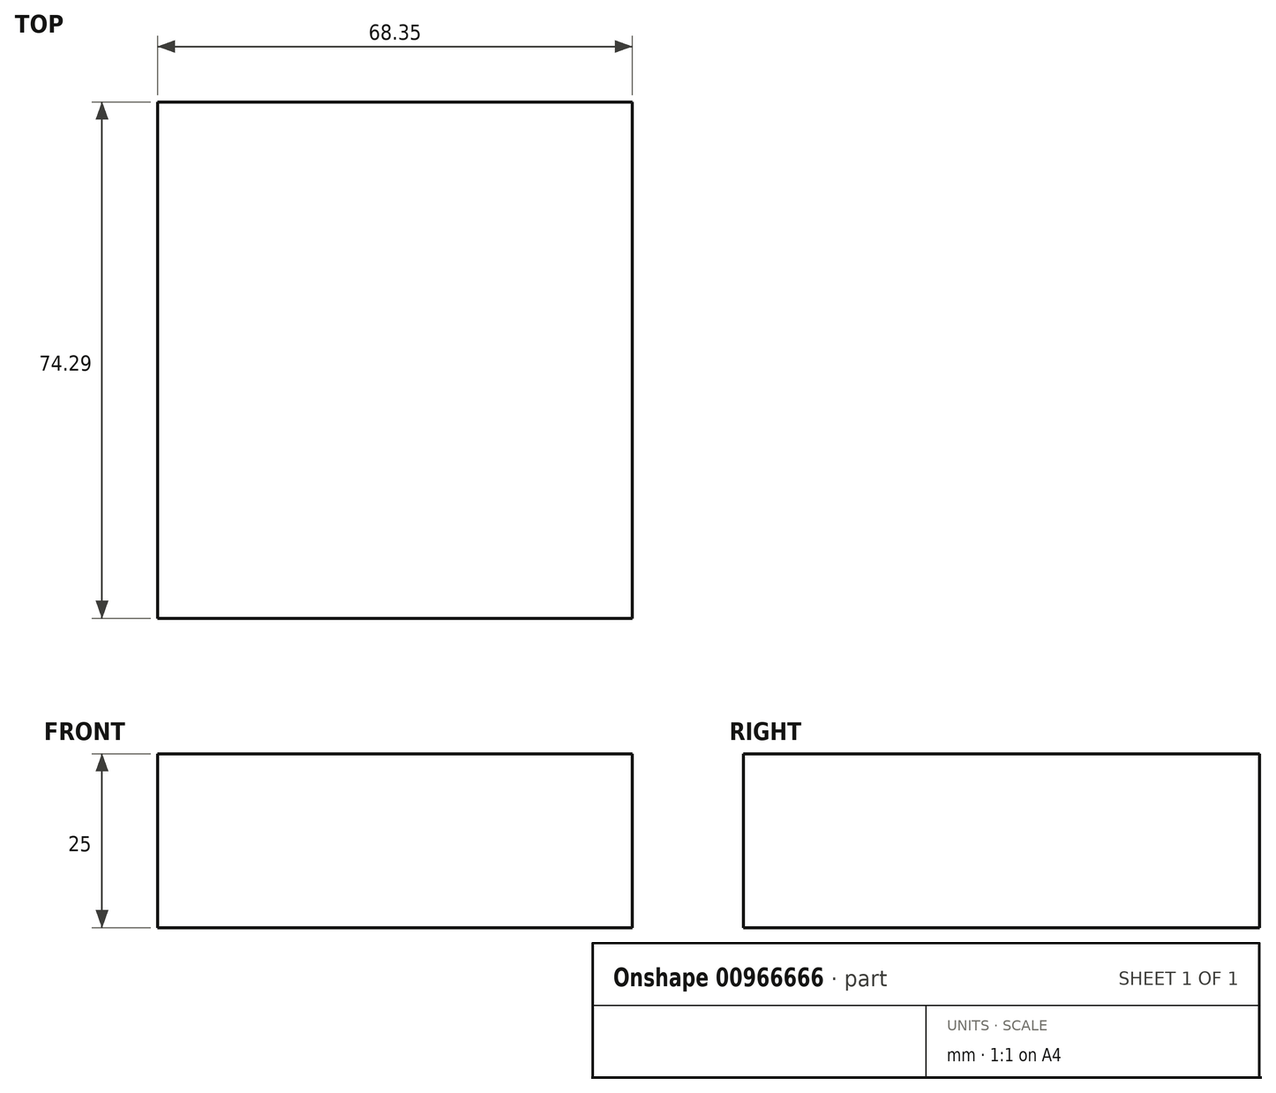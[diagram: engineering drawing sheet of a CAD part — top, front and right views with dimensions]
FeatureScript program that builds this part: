
annotation { "Feature Type Name" : "Feature", "Feature Type Description" : "" }
export const myFeature = defineFeature(function(context is Context, id is Id, definition is map)
    precondition{}
    {
        {
            var Q0;
            Q0=qCreatedBy(makeId("Top.planeOp"),FACE);
            var sketch = newSketch(context, id + "F0", { "sketchPlane" : qUnion([Q0])});
            skLineSegment(sketch, "E0.bottom", {"start": v(-29.84, 33.3) * mm, "end": v(38.5, 33.3) * mm});
            skLineSegment(sketch, "E0.top", {"start": v(-29.84, -40.98) * mm, "end": v(38.5, -40.98) * mm});
            skLineSegment(sketch, "E0.left", {"start": v(-29.84, 33.3) * mm, "end": v(-29.84, -40.98) * mm});
            skLineSegment(sketch, "E0.right", {"start": v(38.5, 33.3) * mm, "end": v(38.5, -40.98) * mm});
            skSolve(sketch);
        }
        {
            var Q0;
            Q0=makeQuery(id+"F0.imprint","IMPRINT",FACE,{"disambiguationData":[TD([[makeQuery(id+"F0.imprint","IMPRINT",EDGE,{"derivedFrom":sQuery(id+"F0.wireOp",EDGE,"E0.bottom")}),-1.0]])]});
            var sketch = newSketch(context, id + "F1", { "sketchPlane" : qUnion([Q0])});
            skSolve(sketch);
        }
        {
            var Q0;
            Q0=makeQuery(id+"F1.imprint","IMPRINT",FACE,{"disambiguationData":[TD([[makeQuery(id+"F1.imprint","IMPRINT",EDGE,{"derivedFrom":makeQuery(id+"F0.imprint","IMPRINT",EDGE,{"derivedFrom":sQuery(id+"F0.wireOp",EDGE,"E0.bottom")})}),-1.0]])]});
            extrude(context, id + "F2", {"entities" : qUnion([Q0]), "depth" : 25 * mm, "offsetDistance" : 25 * mm});
        }
    });
